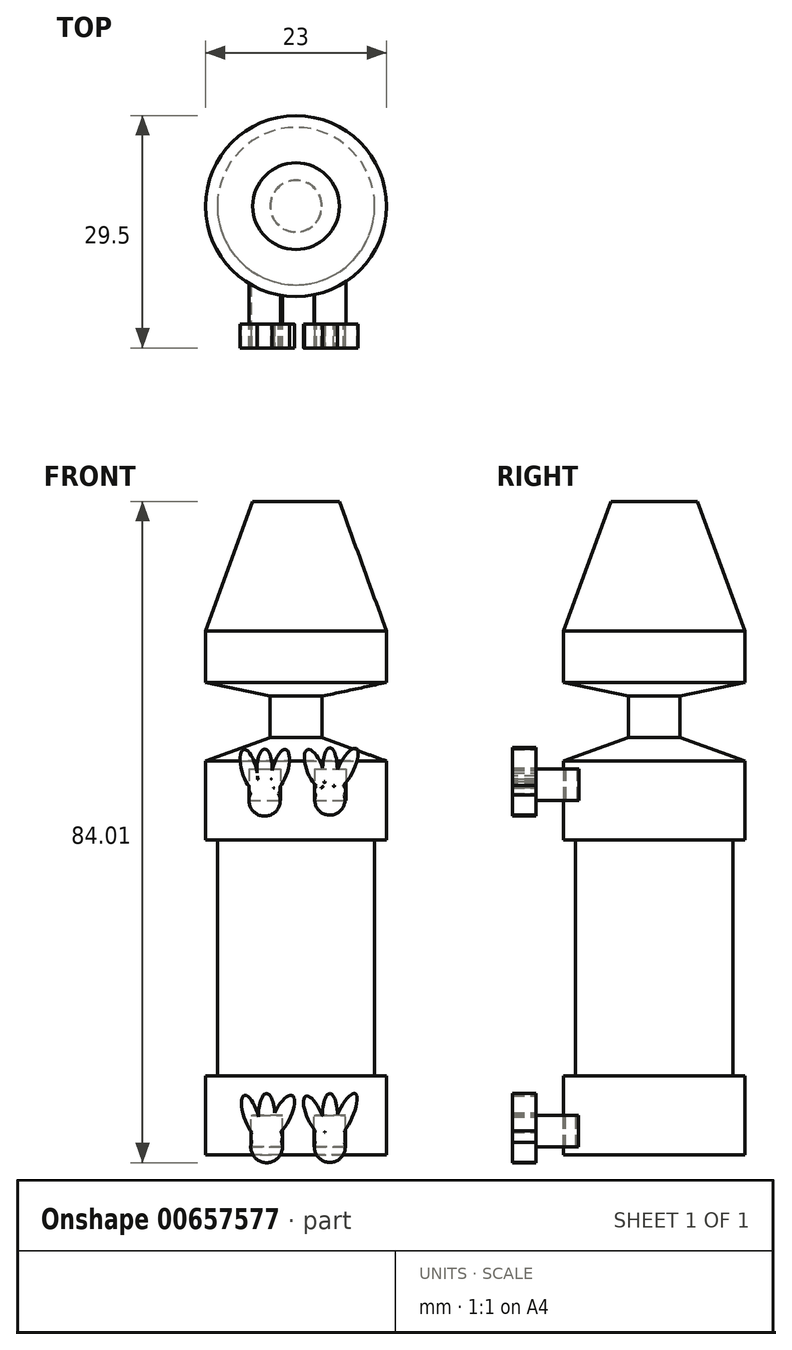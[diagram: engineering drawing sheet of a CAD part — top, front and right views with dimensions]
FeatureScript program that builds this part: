
annotation { "Feature Type Name" : "Feature", "Feature Type Description" : "" }
export const myFeature = defineFeature(function(context is Context, id is Id, definition is map)
    precondition{}
    {
        {
            var Q0;
            Q0=qCreatedBy(makeId("Top.planeOp"),FACE);
            var sketch = newSketch(context, id + "F0", { "sketchPlane" : qUnion([Q0])});
            skCircle(sketch, "E0", {"center": v(0, 0) * mm, "radius": 10 * mm});
            skSolve(sketch);
        }
        {
            var Q0;
            Q0 = qSketchRegion(id + "F0", true);
            extrude(context, id + "F1", {"entities" : qUnion([Q0]), "depth" : 40 * mm, "offsetDistance" : 25 * mm});
        }
        {
            var Q0;
            Q0=makeQuery(id+"F1.opExtrude","CAP_FACE",FACE,{"disambiguationData":[OSD([sQuery(id+"F0.wireOp",EDGE,"E0")])],"isStart":false});
            var sketch = newSketch(context, id + "F2", { "sketchPlane" : qUnion([Q0])});
            skCircle(sketch, "E1", {"center": v(0, 0) * mm, "radius": 11.5 * mm});
            skSolve(sketch);
        }
        {
            var Q0;
            Q0=makeQuery(id+"F2.imprint","IMPRINT",FACE,{"disambiguationData":[TD([[makeQuery(id+"F2.imprint","IMPRINT",EDGE,{"derivedFrom":sQuery(id+"F2.wireOp",EDGE,"E1")}),1.0]])]});
            var Q1;
            Q1=makeQuery(id+"F2.imprint","IMPRINT",FACE,{"disambiguationData":[TD([[makeQuery(id+"F2.imprint","IMPRINT",EDGE,{"derivedFrom":makeQuery(id+"F1.opExtrude","CAP_EDGE",EDGE,{"disambiguationData":[OSD([sQuery(id+"F0.wireOp",EDGE,"E0")])],"isStart":false})}),1.0]])]});
            extrude(context, id + "F3", {"entities" : qUnion([Q0, Q1]), "operationType" : NewBodyOperationType.ADD, "depth" : 5 * mm, "offsetDistance" : 25 * mm});
        }
        {
            var Q0;
            Q0=makeQuery(id+"F3.opExtrude","CAP_FACE",FACE,{"disambiguationData":[OSD([sQuery(id+"F2.wireOp",EDGE,"E1")])],"isStart":true});
            extrude(context, id + "F4", {"entities" : qUnion([Q0]), "operationType" : NewBodyOperationType.ADD, "depth" : 5 * mm, "offsetDistance" : 25 * mm});
        }
        {
            var Q0;
            Q0=makeQuery(id+"F1.opExtrude","CAP_FACE",FACE,{"disambiguationData":[OSD([sQuery(id+"F0.wireOp",EDGE,"E0")])],"isStart":true});
            var sketch = newSketch(context, id + "F5", { "sketchPlane" : qUnion([Q0])});
            skCircle(sketch, "E2", {"center": v(0, 0) * mm, "radius": 11.5 * mm});
            skSolve(sketch);
        }
        {
            var Q0;
            Q0 = qSketchRegion(id + "F5", true);
            extrude(context, id + "F6", {"entities" : qUnion([Q0]), "operationType" : NewBodyOperationType.ADD, "depth" : 5 * mm, "offsetDistance" : 25 * mm});
        }
        {
            var Q0;
            Q0=makeQuery(id+"F6.opExtrude","CAP_FACE",FACE,{"disambiguationData":[OSD([sQuery(id+"F5.wireOp",EDGE,"E2")])],"isStart":true});
            extrude(context, id + "F7", {"entities" : qUnion([Q0]), "operationType" : NewBodyOperationType.ADD, "depth" : 5 * mm, "offsetDistance" : 25 * mm});
        }
        {
            var Q0;
            Q0=makeQuery(id+"F2.imprint","IMPRINT",FACE,{"disambiguationData":[TD([[makeQuery(id+"F2.imprint","IMPRINT",EDGE,{"derivedFrom":makeQuery(id+"F1.opExtrude","CAP_EDGE",EDGE,{"disambiguationData":[OSD([sQuery(id+"F0.wireOp",EDGE,"E0")])],"isStart":false})}),1.0]])]});
            var sketch = newSketch(context, id + "F8", { "sketchPlane" : qUnion([Q0])});
            skLineSegment(sketch, "E3.bottom", {"start": v(-5.99, 0) * mm, "end": v(-1.99, 0) * mm});
            skLineSegment(sketch, "E3.top", {"start": v(-5.99, -15) * mm, "end": v(-1.99, -15) * mm});
            skLineSegment(sketch, "E3.left", {"start": v(-5.99, 0) * mm, "end": v(-5.99, -15) * mm});
            skLineSegment(sketch, "E3.right", {"start": v(-1.99, 0) * mm, "end": v(-1.99, -15) * mm});
            skLineSegment(sketch, "E4.bottom", {"start": v(2.36, 0) * mm, "end": v(6.36, 0) * mm});
            skLineSegment(sketch, "E4.top", {"start": v(2.36, -15) * mm, "end": v(6.36, -15) * mm});
            skLineSegment(sketch, "E4.left", {"start": v(2.36, 0) * mm, "end": v(2.36, -15) * mm});
            skLineSegment(sketch, "E4.right", {"start": v(6.36, 0) * mm, "end": v(6.36, -15) * mm});
            skSolve(sketch);
        }
        {
            var Q0;
            Q0 = qSketchRegion(id + "F8", true);
            extrude(context, id + "F9", {"entities" : qUnion([Q0]), "operationType" : NewBodyOperationType.ADD, "depth" : 4 * mm, "offsetDistance" : 25 * mm});
        }
        {
            var Q0;
            Q0=makeQuery(id+"F9.opExtrude","SWEPT_FACE",FACE,{"disambiguationData":[OSD([sQuery(id+"F8.wireOp",EDGE,"E3.top")])]});
            var sketch = newSketch(context, id + "F10", { "sketchPlane" : qUnion([Q0])});
            skCircle(sketch, "E5", {"center": v(-3.99, 40) * mm, "radius": 2 * mm});
            skEllipse(sketch, "E6", {"center": v(-5.99, 44) * mm, "majorRadius": 2.55 * mm, "minorRadius": 0.93 * mm, "majorAxis": v(-0.26, 0.97)});
            skEllipse(sketch, "E7", {"center": v(-3.99, 44) * mm, "majorRadius": 2.52 * mm, "minorRadius": 0.97 * mm, "majorAxis": v(0, 1)});
            skEllipse(sketch, "E8", {"center": v(-1.99, 44) * mm, "majorRadius": 2.56 * mm, "minorRadius": 0.96 * mm, "majorAxis": v(0.27, 0.96)});
            skEllipse(sketch, "E9", {"center": v(-3.99, 41.48) * mm, "majorRadius": 1.98 * mm, "minorRadius": 1.35 * mm, "majorAxis": v(-1, 0)});
            skCircle(sketch, "E10", {"center": v(4.3, 40.05) * mm, "radius": 1.92 * mm});
            skEllipse(sketch, "E11", {"center": v(2.36, 44.04) * mm, "majorRadius": 2.58 * mm, "minorRadius": 1 * mm, "majorAxis": v(-0.36, 0.93)});
            skEllipse(sketch, "E12", {"center": v(4.32, 43.98) * mm, "majorRadius": 2.73 * mm, "minorRadius": 0.93 * mm, "majorAxis": v(0, 1)});
            skEllipse(sketch, "E13", {"center": v(6.33, 44.02) * mm, "majorRadius": 2.89 * mm, "minorRadius": 0.95 * mm, "majorAxis": v(0.46, 0.9)});
            skEllipse(sketch, "E14", {"center": v(4.32, 41.25) * mm, "majorRadius": 1.97 * mm, "minorRadius": 1.26 * mm, "majorAxis": v(-1, 0)});
            skSolve(sketch);
        }
        {
            var Q0;
            {var subQ0=sQuery(id+"F10.wireOp",EDGE,"E9");var subQ1=sQuery(id+"F10.wireOp",EDGE,"E6");var subQ2=makeQuery(id+"F10.imprint","INTERSECT",VERTEX,{"disambiguationData":[OD(0.0)],"derivedFrom":[subQ1,subQ0]});Q0=makeQuery(id+"F10.imprint","IMPRINT",FACE,{"disambiguationData":[TD([[makeQuery(id+"F10.imprint","IMPRINT",EDGE,{"disambiguationData":[TD([[subQ2,-1.0]])],"derivedFrom":subQ1}),1.0]])]});}
            var Q1;
            {var subQ0=sQuery(id+"F10.wireOp",EDGE,"E7");var subQ1=sQuery(id+"F10.wireOp",EDGE,"E6");var subQ2=makeQuery(id+"F10.imprint","INTERSECT",VERTEX,{"disambiguationData":[OD(0.0)],"derivedFrom":[subQ1,subQ0]});Q1=makeQuery(id+"F10.imprint","IMPRINT",FACE,{"disambiguationData":[TD([[makeQuery(id+"F10.imprint","IMPRINT",EDGE,{"disambiguationData":[TD([[subQ2,-1.0]])],"derivedFrom":subQ1}),1.0]])]});}
            var Q2;
            {var subQ0=sQuery(id+"F10.wireOp",EDGE,"E8");var subQ1=sQuery(id+"F10.wireOp",EDGE,"E7");var subQ2=makeQuery(id+"F10.imprint","INTERSECT",VERTEX,{"disambiguationData":[OD(0.0)],"derivedFrom":[subQ1,subQ0]});Q2=makeQuery(id+"F10.imprint","IMPRINT",FACE,{"disambiguationData":[TD([[makeQuery(id+"F10.imprint","IMPRINT",EDGE,{"disambiguationData":[TD([[subQ2,-1.0]])],"derivedFrom":subQ1}),1.0]])]});}
            var Q3;
            {var subQ0=sQuery(id+"F10.wireOp",EDGE,"E9");var subQ1=sQuery(id+"F10.wireOp",EDGE,"E5");var subQ2=makeQuery(id+"F10.imprint","INTERSECT",VERTEX,{"disambiguationData":[OD(0.0)],"derivedFrom":[subQ1,subQ0]});Q3=makeQuery(id+"F10.imprint","IMPRINT",FACE,{"disambiguationData":[TD([[makeQuery(id+"F10.imprint","IMPRINT",EDGE,{"disambiguationData":[TD([[subQ2,-1.0]])],"derivedFrom":subQ1}),-1.0]])]});}
            var Q4;
            {var subQ0=sQuery(id+"F10.wireOp",EDGE,"E8");var subQ1=sQuery(id+"F10.wireOp",EDGE,"E5");var subQ2=makeQuery(id+"F10.imprint","INTERSECT",VERTEX,{"disambiguationData":[OD(0.0)],"derivedFrom":[subQ1,subQ0]});Q4=makeQuery(id+"F10.imprint","IMPRINT",FACE,{"disambiguationData":[TD([[makeQuery(id+"F10.imprint","IMPRINT",EDGE,{"disambiguationData":[TD([[subQ2,-1.0]])],"derivedFrom":subQ1}),-1.0]])]});}
            var Q5;
            {var subQ3=sQuery(id+"F10.wireOp",EDGE,"E7");var subQ5=sQuery(id+"F10.wireOp",EDGE,"E5");var subQ6=makeQuery(id+"F10.imprint","INTERSECT",VERTEX,{"disambiguationData":[OD(1.0)],"derivedFrom":[subQ5,subQ3]});Q5=makeQuery(id+"F10.imprint","IMPRINT",FACE,{"disambiguationData":[TD([[makeQuery(id+"F10.imprint","IMPRINT",EDGE,{"disambiguationData":[TD([[subQ6,-1.0]])],"derivedFrom":subQ5}),-1.0]])]});}
            var Q6;
            {var subQ1=sQuery(id+"F10.wireOp",EDGE,"E5");var subQ3=sQuery(id+"F10.wireOp",EDGE,"E9");var subQ8=makeQuery(id+"F10.imprint","INTERSECT",VERTEX,{"disambiguationData":[OD(0.0)],"derivedFrom":[subQ1,subQ3]});Q6=makeQuery(id+"F10.imprint","IMPRINT",FACE,{"disambiguationData":[TD([[makeQuery(id+"F10.imprint","IMPRINT",EDGE,{"disambiguationData":[TD([[subQ8,-1.0]])],"derivedFrom":subQ1}),1.0]])]});}
            var Q7;
            {var subQ0=sQuery(id+"F10.wireOp",EDGE,"E5");var subQ1=makeQuery(id+"F9.opExtrude","CAP_EDGE",EDGE,{"disambiguationData":[OSD([sQuery(id+"F8.wireOp",EDGE,"E3.top")])],"isStart":true});var subQ2=makeQuery(id+"F10.imprint","INTERSECT",VERTEX,{"disambiguationData":[OD(0.0)],"derivedFrom":[subQ1,subQ0]});Q7=makeQuery(id+"F10.imprint","IMPRINT",FACE,{"disambiguationData":[TD([[makeQuery(id+"F10.imprint","IMPRINT",EDGE,{"disambiguationData":[TD([[subQ2,1.0]])],"derivedFrom":subQ0}),1.0]])]});}
            var Q8;
            {var subQ0=sQuery(id+"F10.wireOp",EDGE,"E7");var subQ1=makeQuery(id+"F9.opExtrude","CAP_EDGE",EDGE,{"disambiguationData":[OSD([sQuery(id+"F8.wireOp",EDGE,"E3.top")])],"isStart":false});var subQ2=makeQuery(id+"F10.imprint","INTERSECT",VERTEX,{"disambiguationData":[OD(0.0)],"derivedFrom":[subQ1,subQ0]});Q8=makeQuery(id+"F10.imprint","IMPRINT",FACE,{"disambiguationData":[TD([[makeQuery(id+"F10.imprint","IMPRINT",EDGE,{"disambiguationData":[TD([[subQ2,1.0]])],"derivedFrom":subQ0}),1.0]])]});}
            var Q9;
            {var subQ0=sQuery(id+"F10.wireOp",EDGE,"E9");var subQ1=sQuery(id+"F10.wireOp",EDGE,"E5");var subQ2=makeQuery(id+"F10.imprint","INTERSECT",VERTEX,{"disambiguationData":[OD(0.0)],"derivedFrom":[subQ1,subQ0]});Q9=makeQuery(id+"F10.imprint","IMPRINT",FACE,{"disambiguationData":[TD([[makeQuery(id+"F10.imprint","IMPRINT",EDGE,{"disambiguationData":[TD([[subQ2,1.0]])],"derivedFrom":subQ1}),1.0]])]});}
            var Q10;
            {var subQ0=sQuery(id+"F10.wireOp",EDGE,"E6");var subQ1=sQuery(id+"F8.wireOp",EDGE,"E3.top");var subQ4=makeQuery(id+"F9.opExtrude","CAP_EDGE",EDGE,{"disambiguationData":[OSD([subQ1])],"isStart":false});var subQ5=makeQuery(id+"F10.imprint","INTERSECT",VERTEX,{"derivedFrom":[subQ4,subQ0]});Q10=makeQuery(id+"F10.imprint","IMPRINT",FACE,{"disambiguationData":[TD([[makeQuery(id+"F10.imprint","IMPRINT",EDGE,{"disambiguationData":[TD([[subQ5,-1.0]])],"derivedFrom":subQ0}),1.0]])]});}
            var Q11;
            {var subQ1=sQuery(id+"F10.wireOp",EDGE,"E6");var subQ7=sQuery(id+"F10.wireOp",EDGE,"E9");var subQ8=makeQuery(id+"F10.imprint","INTERSECT",VERTEX,{"disambiguationData":[OD(1.0)],"derivedFrom":[subQ1,subQ7]});Q11=makeQuery(id+"F10.imprint","IMPRINT",FACE,{"disambiguationData":[TD([[makeQuery(id+"F10.imprint","IMPRINT",EDGE,{"disambiguationData":[TD([[subQ8,-1.0]])],"derivedFrom":subQ1}),1.0]])]});}
            var Q12;
            {var subQ1=sQuery(id+"F10.wireOp",EDGE,"E8");var subQ6=sQuery(id+"F10.wireOp",EDGE,"E7");var subQ10=makeQuery(id+"F10.imprint","INTERSECT",VERTEX,{"disambiguationData":[OD(0.0)],"derivedFrom":[subQ6,subQ1]});Q12=makeQuery(id+"F10.imprint","IMPRINT",FACE,{"disambiguationData":[TD([[makeQuery(id+"F10.imprint","IMPRINT",EDGE,{"disambiguationData":[TD([[subQ10,-1.0]])],"derivedFrom":subQ6}),-1.0]])]});}
            var Q13;
            {var subQ0=sQuery(id+"F10.wireOp",EDGE,"E8");var subQ1=sQuery(id+"F8.wireOp",EDGE,"E3.top");var subQ2=makeQuery(id+"F9.opExtrude","CAP_EDGE",EDGE,{"disambiguationData":[OSD([subQ1])],"isStart":false});var subQ3=makeQuery(id+"F10.imprint","INTERSECT",VERTEX,{"derivedFrom":[subQ2,subQ0]});Q13=makeQuery(id+"F10.imprint","IMPRINT",FACE,{"disambiguationData":[TD([[makeQuery(id+"F10.imprint","IMPRINT",EDGE,{"disambiguationData":[TD([[subQ3,1.0]])],"derivedFrom":subQ0}),1.0]])]});}
            var Q14;
            {var subQ1=sQuery(id+"F10.wireOp",EDGE,"E7");var subQ5=sQuery(id+"F10.wireOp",EDGE,"E6");var subQ11=makeQuery(id+"F10.imprint","INTERSECT",VERTEX,{"disambiguationData":[OD(0.0)],"derivedFrom":[subQ5,subQ1]});Q14=makeQuery(id+"F10.imprint","IMPRINT",FACE,{"disambiguationData":[TD([[makeQuery(id+"F10.imprint","IMPRINT",EDGE,{"disambiguationData":[TD([[subQ11,-1.0]])],"derivedFrom":subQ5}),-1.0]])]});}
            var Q15;
            {var subQ0=sQuery(id+"F10.wireOp",EDGE,"E7");var subQ1=sQuery(id+"F10.wireOp",EDGE,"E5");var subQ2=makeQuery(id+"F10.imprint","INTERSECT",VERTEX,{"disambiguationData":[OD(0.0)],"derivedFrom":[subQ1,subQ0]});Q15=makeQuery(id+"F10.imprint","IMPRINT",FACE,{"disambiguationData":[TD([[makeQuery(id+"F10.imprint","IMPRINT",EDGE,{"disambiguationData":[TD([[subQ2,-1.0]])],"derivedFrom":subQ1}),-1.0]])]});}
            var Q16;
            {var subQ0=sQuery(id+"F10.wireOp",EDGE,"E8");var subQ1=sQuery(id+"F10.wireOp",EDGE,"E5");var subQ2=makeQuery(id+"F10.imprint","INTERSECT",VERTEX,{"disambiguationData":[OD(1.0)],"derivedFrom":[subQ1,subQ0]});Q16=makeQuery(id+"F10.imprint","IMPRINT",FACE,{"disambiguationData":[TD([[makeQuery(id+"F10.imprint","IMPRINT",EDGE,{"disambiguationData":[TD([[subQ2,-1.0]])],"derivedFrom":subQ1}),-1.0]])]});}
            var Q17;
            {var subQ0=sQuery(id+"F10.wireOp",EDGE,"E7");var subQ1=sQuery(id+"F10.wireOp",EDGE,"E5");var subQ2=makeQuery(id+"F10.imprint","INTERSECT",VERTEX,{"disambiguationData":[OD(0.0)],"derivedFrom":[subQ1,subQ0]});Q17=makeQuery(id+"F10.imprint","IMPRINT",FACE,{"disambiguationData":[TD([[makeQuery(id+"F10.imprint","IMPRINT",EDGE,{"disambiguationData":[TD([[subQ2,-1.0]])],"derivedFrom":subQ1}),1.0]])]});}
            var Q18;
            {var subQ0=sQuery(id+"F10.wireOp",EDGE,"E13");var subQ1=sQuery(id+"F10.wireOp",EDGE,"E12");var subQ2=makeQuery(id+"F10.imprint","INTERSECT",VERTEX,{"disambiguationData":[OD(0.0)],"derivedFrom":[subQ1,subQ0]});Q18=makeQuery(id+"F10.imprint","IMPRINT",FACE,{"disambiguationData":[TD([[makeQuery(id+"F10.imprint","IMPRINT",EDGE,{"disambiguationData":[TD([[subQ2,1.0]])],"derivedFrom":subQ1}),-1.0]])]});}
            var Q19;
            {var subQ0=sQuery(id+"F10.wireOp",EDGE,"E13");var subQ1=sQuery(id+"F10.wireOp",EDGE,"E12");var subQ2=makeQuery(id+"F10.imprint","INTERSECT",VERTEX,{"disambiguationData":[OD(0.0)],"derivedFrom":[subQ1,subQ0]});Q19=makeQuery(id+"F10.imprint","IMPRINT",FACE,{"disambiguationData":[TD([[makeQuery(id+"F10.imprint","IMPRINT",EDGE,{"disambiguationData":[TD([[subQ2,1.0]])],"derivedFrom":subQ1}),1.0]])]});}
            var Q20;
            {var subQ0=sQuery(id+"F10.wireOp",EDGE,"E13");var subQ1=sQuery(id+"F10.wireOp",EDGE,"E10");var subQ2=makeQuery(id+"F10.imprint","INTERSECT",VERTEX,{"disambiguationData":[OD(0.0)],"derivedFrom":[subQ1,subQ0]});Q20=makeQuery(id+"F10.imprint","IMPRINT",FACE,{"disambiguationData":[TD([[makeQuery(id+"F10.imprint","IMPRINT",EDGE,{"disambiguationData":[TD([[subQ2,-1.0]])],"derivedFrom":subQ1}),-1.0]])]});}
            var Q21;
            {var subQ0=sQuery(id+"F10.wireOp",EDGE,"E12");var subQ1=sQuery(id+"F10.wireOp",EDGE,"E10");var subQ2=makeQuery(id+"F10.imprint","INTERSECT",VERTEX,{"disambiguationData":[OD(0.0)],"derivedFrom":[subQ1,subQ0]});Q21=makeQuery(id+"F10.imprint","IMPRINT",FACE,{"disambiguationData":[TD([[makeQuery(id+"F10.imprint","IMPRINT",EDGE,{"disambiguationData":[TD([[subQ2,-1.0]])],"derivedFrom":subQ1}),-1.0]])]});}
            var Q22;
            {var subQ0=sQuery(id+"F10.wireOp",EDGE,"E13");var subQ1=sQuery(id+"F10.wireOp",EDGE,"E10");var subQ2=makeQuery(id+"F10.imprint","INTERSECT",VERTEX,{"disambiguationData":[OD(0.0)],"derivedFrom":[subQ1,subQ0]});Q22=makeQuery(id+"F10.imprint","IMPRINT",FACE,{"disambiguationData":[TD([[makeQuery(id+"F10.imprint","IMPRINT",EDGE,{"disambiguationData":[TD([[subQ2,-1.0]])],"derivedFrom":subQ1}),1.0]])]});}
            var Q23;
            {var subQ0=sQuery(id+"F10.wireOp",EDGE,"E13");var subQ1=sQuery(id+"F10.wireOp",EDGE,"E10");var subQ2=makeQuery(id+"F10.imprint","INTERSECT",VERTEX,{"disambiguationData":[OD(1.0)],"derivedFrom":[subQ1,subQ0]});Q23=makeQuery(id+"F10.imprint","IMPRINT",FACE,{"disambiguationData":[TD([[makeQuery(id+"F10.imprint","IMPRINT",EDGE,{"disambiguationData":[TD([[subQ2,-1.0]])],"derivedFrom":subQ1}),1.0]])]});}
            var Q24;
            {var subQ1=sQuery(id+"F10.wireOp",EDGE,"E10");var subQ7=sQuery(id+"F10.wireOp",EDGE,"E13");var subQ8=makeQuery(id+"F10.imprint","INTERSECT",VERTEX,{"disambiguationData":[OD(1.0)],"derivedFrom":[subQ1,subQ7]});Q24=makeQuery(id+"F10.imprint","IMPRINT",FACE,{"disambiguationData":[TD([[makeQuery(id+"F10.imprint","IMPRINT",EDGE,{"disambiguationData":[TD([[subQ8,-1.0]])],"derivedFrom":subQ1}),-1.0]])]});}
            var Q25;
            {var subQ0=sQuery(id+"F10.wireOp",EDGE,"E12");var subQ1=sQuery(id+"F10.wireOp",EDGE,"E11");var subQ2=makeQuery(id+"F10.imprint","INTERSECT",VERTEX,{"disambiguationData":[OD(0.0)],"derivedFrom":[subQ1,subQ0]});Q25=makeQuery(id+"F10.imprint","IMPRINT",FACE,{"disambiguationData":[TD([[makeQuery(id+"F10.imprint","IMPRINT",EDGE,{"disambiguationData":[TD([[subQ2,1.0]])],"derivedFrom":subQ1}),-1.0]])]});}
            var Q26;
            {var subQ1=sQuery(id+"F10.wireOp",EDGE,"E11");var subQ3=sQuery(id+"F10.wireOp",EDGE,"E10");var subQ8=makeQuery(id+"F10.imprint","INTERSECT",VERTEX,{"disambiguationData":[OD(0.0)],"derivedFrom":[subQ3,subQ1]});Q26=makeQuery(id+"F10.imprint","IMPRINT",FACE,{"disambiguationData":[TD([[makeQuery(id+"F10.imprint","IMPRINT",EDGE,{"disambiguationData":[TD([[subQ8,-1.0]])],"derivedFrom":subQ3}),-1.0]])]});}
            var Q27;
            {var subQ0=sQuery(id+"F10.wireOp",EDGE,"E14");var subQ1=sQuery(id+"F10.wireOp",EDGE,"E11");var subQ2=makeQuery(id+"F10.imprint","INTERSECT",VERTEX,{"disambiguationData":[OD(0.0)],"derivedFrom":[subQ1,subQ0]});Q27=makeQuery(id+"F10.imprint","IMPRINT",FACE,{"disambiguationData":[TD([[makeQuery(id+"F10.imprint","IMPRINT",EDGE,{"disambiguationData":[TD([[subQ2,1.0]])],"derivedFrom":subQ1}),1.0]])]});}
            var Q28;
            {var subQ0=sQuery(id+"F10.wireOp",EDGE,"E14");var subQ1=sQuery(id+"F10.wireOp",EDGE,"E10");var subQ2=makeQuery(id+"F10.imprint","INTERSECT",VERTEX,{"disambiguationData":[OD(1.0)],"derivedFrom":[subQ1,subQ0]});Q28=makeQuery(id+"F10.imprint","IMPRINT",FACE,{"disambiguationData":[TD([[makeQuery(id+"F10.imprint","IMPRINT",EDGE,{"disambiguationData":[TD([[subQ2,1.0]])],"derivedFrom":subQ1}),-1.0]])]});}
            var Q29;
            {var subQ0=sQuery(id+"F10.wireOp",EDGE,"E14");var subQ1=sQuery(id+"F10.wireOp",EDGE,"E10");var subQ9=makeQuery(id+"F10.imprint","INTERSECT",VERTEX,{"disambiguationData":[OD(0.0)],"derivedFrom":[subQ1,subQ0]});Q29=makeQuery(id+"F10.imprint","IMPRINT",FACE,{"disambiguationData":[TD([[makeQuery(id+"F10.imprint","IMPRINT",EDGE,{"disambiguationData":[TD([[subQ9,-1.0]])],"derivedFrom":subQ1}),1.0]])]});}
            var Q30;
            {var subQ0=sQuery(id+"F10.wireOp",EDGE,"E14");var subQ1=sQuery(id+"F10.wireOp",EDGE,"E10");var subQ2=makeQuery(id+"F10.imprint","INTERSECT",VERTEX,{"disambiguationData":[OD(0.0)],"derivedFrom":[subQ1,subQ0]});Q30=makeQuery(id+"F10.imprint","IMPRINT",FACE,{"disambiguationData":[TD([[makeQuery(id+"F10.imprint","IMPRINT",EDGE,{"disambiguationData":[TD([[subQ2,-1.0]])],"derivedFrom":subQ1}),-1.0]])]});}
            var Q31;
            {var subQ0=sQuery(id+"F10.wireOp",EDGE,"E14");var subQ1=sQuery(id+"F10.wireOp",EDGE,"E10");var subQ2=makeQuery(id+"F10.imprint","INTERSECT",VERTEX,{"disambiguationData":[OD(0.0)],"derivedFrom":[subQ1,subQ0]});Q31=makeQuery(id+"F10.imprint","IMPRINT",FACE,{"disambiguationData":[TD([[makeQuery(id+"F10.imprint","IMPRINT",EDGE,{"disambiguationData":[TD([[subQ2,1.0]])],"derivedFrom":subQ1}),1.0]])]});}
            var Q32;
            {var subQ0=sQuery(id+"F10.wireOp",EDGE,"E12");var subQ1=sQuery(id+"F10.wireOp",EDGE,"E11");var subQ2=makeQuery(id+"F10.imprint","INTERSECT",VERTEX,{"disambiguationData":[OD(0.0)],"derivedFrom":[subQ1,subQ0]});Q32=makeQuery(id+"F10.imprint","IMPRINT",FACE,{"disambiguationData":[TD([[makeQuery(id+"F10.imprint","IMPRINT",EDGE,{"disambiguationData":[TD([[subQ2,1.0]])],"derivedFrom":subQ1}),1.0]])]});}
            var Q33;
            {var subQ0=sQuery(id+"F10.wireOp",EDGE,"E12");var subQ1=sQuery(id+"F10.wireOp",EDGE,"E10");var subQ2=makeQuery(id+"F10.imprint","INTERSECT",VERTEX,{"disambiguationData":[OD(1.0)],"derivedFrom":[subQ1,subQ0]});Q33=makeQuery(id+"F10.imprint","IMPRINT",FACE,{"disambiguationData":[TD([[makeQuery(id+"F10.imprint","IMPRINT",EDGE,{"disambiguationData":[TD([[subQ2,-1.0]])],"derivedFrom":subQ1}),-1.0]])]});}
            extrude(context, id + "F11", {"entities" : qUnion([Q0, Q1, Q2, Q3, Q4, Q5, Q6, Q7, Q8, Q9, Q10, Q11, Q12, Q13, Q14, Q15, Q16, Q17, Q18, Q19, Q20, Q21, Q22, Q23, Q24, Q25, Q26, Q27, Q28, Q29, Q30, Q31, Q32, Q33]), "operationType" : NewBodyOperationType.ADD, "depth" : 3 * mm, "offsetDistance" : 25 * mm});
        }
        {
            var Q0;
            Q0=makeQuery(id+"F3.opExtrude","CAP_FACE",FACE,{"disambiguationData":[OSD([sQuery(id+"F2.wireOp",EDGE,"E1")])],"isStart":false});
            var sketch = newSketch(context, id + "F12", { "sketchPlane" : qUnion([Q0])});
            skCircle(sketch, "E15", {"center": v(0, 0) * mm, "radius": 11.5 * mm});
            skSolve(sketch);
        }
        {
            var Q0;
            Q0 = qSketchRegion(id + "F12", true);
            extrude(context, id + "F13", {"entities" : qUnion([Q0]), "operationType" : NewBodyOperationType.ADD, "depth" : 3 * mm, "offsetDistance" : 25 * mm, "hasDraft" : true, "draftAngle" : 70 * degree, "draftPullDirection" : true});
        }
        {
            var Q0;
            Q0=makeQuery(id+"F13.opExtrude","CAP_FACE",FACE,{"disambiguationData":[OSD([sQuery(id+"F12.wireOp",EDGE,"E15")])],"isStart":false});
            var sketch = newSketch(context, id + "F14", { "sketchPlane" : qUnion([Q0])});
            skCircle(sketch, "E16", {"center": v(0, 0) * mm, "radius": 3.3 * mm});
            skSolve(sketch);
        }
        {
            var Q0;
            Q0 = qSketchRegion(id + "F14", true);
            extrude(context, id + "F15", {"entities" : qUnion([Q0]), "operationType" : NewBodyOperationType.ADD, "depth" : 5 * mm, "offsetDistance" : 25 * mm});
        }
        {
            var Q0;
            Q0=makeQuery(id+"F15.opExtrude","CAP_FACE",FACE,{"disambiguationData":[OSD([sQuery(id+"F14.wireOp",EDGE,"E16")])],"isStart":false});
            var sketch = newSketch(context, id + "F16", { "sketchPlane" : qUnion([Q0])});
            skCircle(sketch, "E17", {"center": v(0, 0) * mm, "radius": 11.5 * mm});
            skSolve(sketch);
        }
        {
            var Q0;
            Q0 = qSketchRegion(id + "F16", true);
            extrude(context, id + "F17", {"entities" : qUnion([Q0]), "operationType" : NewBodyOperationType.ADD, "depth" : 25 * mm, "offsetDistance" : 25 * mm});
        }
        {
            var Q0;
            Q0=makeQuery(id+"F17.opExtrude","CAP_EDGE",EDGE,{"disambiguationData":[OSD([sQuery(id+"F16.wireOp",EDGE,"E17")])],"isStart":true});
            chamfer(context, id + "F18", {"entities" : qUnion([Q0]), "chamferType" : ChamferType.OFFSET_ANGLE, "width" : 2 * mm, "oppositeDirection" : false, "angle" : 78 * degree, "tangentPropagation" : true});
        }
        {
            var Q0;
            Q0=makeQuery(id+"F17.opExtrude","CAP_EDGE",EDGE,{"disambiguationData":[OSD([sQuery(id+"F16.wireOp",EDGE,"E17")])],"isStart":false});
            chamfer(context, id + "F19", {"entities" : qUnion([Q0]), "chamferType" : ChamferType.OFFSET_ANGLE, "width" : 6 * mm, "oppositeDirection" : false, "angle" : 70 * degree, "tangentPropagation" : true});
        }
        {
            var Q0;
            Q0=makeQuery(id+"F5.imprint","IMPRINT",FACE,{"disambiguationData":[TD([[makeQuery(id+"F5.imprint","IMPRINT",EDGE,{"derivedFrom":makeQuery(id+"F1.opExtrude","CAP_EDGE",EDGE,{"disambiguationData":[OSD([sQuery(id+"F0.wireOp",EDGE,"E0")])],"isStart":true})}),-1.0]])]});
            var sketch = newSketch(context, id + "F20", { "sketchPlane" : qUnion([Q0])});
            skLineSegment(sketch, "E18.bottom", {"start": v(-5.74, 0) * mm, "end": v(-1.74, 0) * mm});
            skLineSegment(sketch, "E18.top", {"start": v(-5.74, 15) * mm, "end": v(-1.74, 15) * mm});
            skLineSegment(sketch, "E18.left", {"start": v(-5.74, 0) * mm, "end": v(-5.74, 15) * mm});
            skLineSegment(sketch, "E18.right", {"start": v(-1.74, 0) * mm, "end": v(-1.74, 15) * mm});
            skLineSegment(sketch, "E19.bottom", {"start": v(2.26, 0) * mm, "end": v(6.26, 0) * mm});
            skLineSegment(sketch, "E19.top", {"start": v(2.26, 15) * mm, "end": v(6.26, 15) * mm});
            skLineSegment(sketch, "E19.left", {"start": v(2.26, 0) * mm, "end": v(2.26, 15) * mm});
            skLineSegment(sketch, "E19.right", {"start": v(6.26, 0) * mm, "end": v(6.26, 15) * mm});
            skSolve(sketch);
        }
        {
            var Q0;
            Q0 = qSketchRegion(id + "F20", true);
            extrude(context, id + "F21", {"entities" : qUnion([Q0]), "operationType" : NewBodyOperationType.ADD, "depth" : 4 * mm, "offsetDistance" : 25 * mm});
        }
        {
            var Q0;
            Q0=makeQuery(id+"F21.opExtrude","SWEPT_FACE",FACE,{"disambiguationData":[OSD([sQuery(id+"F20.wireOp",EDGE,"E18.top")])]});
            var sketch = newSketch(context, id + "F22", { "sketchPlane" : qUnion([Q0])});
            skCircle(sketch, "E20", {"center": v(-3.74, -4) * mm, "radius": 2.01 * mm});
            skCircle(sketch, "E21", {"center": v(4.3, -4) * mm, "radius": 1.97 * mm});
            skEllipse(sketch, "E22", {"center": v(-5.74, 0) * mm, "majorRadius": 2.68 * mm, "minorRadius": 0.9 * mm, "majorAxis": v(-0.3, 0.95)});
            skEllipse(sketch, "E23", {"center": v(-3.74, 0) * mm, "majorRadius": 2.77 * mm, "minorRadius": 1.02 * mm, "majorAxis": v(0, 1)});
            skEllipse(sketch, "E24", {"center": v(-1.74, 0) * mm, "majorRadius": 2.8 * mm, "minorRadius": 1.03 * mm, "majorAxis": v(0.45, 0.9)});
            skEllipse(sketch, "E25", {"center": v(-3.74, -2.77) * mm, "majorRadius": 2 * mm, "minorRadius": 1.67 * mm, "majorAxis": v(-1, 0)});
            skPoint(sketch, "E25.majorAxisSnap0", {"position": v(-3.74, -2.77) * mm});
            skPoint(sketch, "E25.majorAxisSnap1", {"position": v(-5.74, -2) * mm});
            skEllipse(sketch, "E26", {"center": v(2.32, 0) * mm, "majorRadius": 2.66 * mm, "minorRadius": 0.93 * mm, "majorAxis": v(-0.4, 0.91)});
            skEllipse(sketch, "E27", {"center": v(4.3, 0) * mm, "majorRadius": 2.77 * mm, "minorRadius": 0.96 * mm, "majorAxis": v(0, 1)});
            skEllipse(sketch, "E28", {"center": v(6.23, 0) * mm, "majorRadius": 3.05 * mm, "minorRadius": 0.93 * mm, "majorAxis": v(0.42, 0.9)});
            skEllipse(sketch, "E29", {"center": v(4.3, -2.77) * mm, "majorRadius": 1.96 * mm, "minorRadius": 2.63 * mm, "majorAxis": v(-1, 0)});
            skSolve(sketch);
        }
        {
            var Q0;
            Q0 = qSketchRegion(id + "F22", true);
            var Q1;
            {var subQ0=sQuery(id+"F22.wireOp",EDGE,"E24");var subQ1=sQuery(id+"F22.wireOp",EDGE,"E20");var subQ2=makeQuery(id+"F22.imprint","INTERSECT",VERTEX,{"disambiguationData":[OD(1.0)],"derivedFrom":[subQ1,subQ0]});Q1=makeQuery(id+"F22.imprint","IMPRINT",FACE,{"disambiguationData":[TD([[makeQuery(id+"F22.imprint","IMPRINT",EDGE,{"disambiguationData":[TD([[subQ2,-1.0]])],"derivedFrom":subQ1}),-1.0]])]});}
            var Q2;
            {var subQ0=sQuery(id+"F22.wireOp",EDGE,"E23");var subQ1=sQuery(id+"F22.wireOp",EDGE,"E20");var subQ2=makeQuery(id+"F22.imprint","INTERSECT",VERTEX,{"disambiguationData":[OD(0.0)],"derivedFrom":[subQ1,subQ0]});Q2=makeQuery(id+"F22.imprint","IMPRINT",FACE,{"disambiguationData":[TD([[makeQuery(id+"F22.imprint","IMPRINT",EDGE,{"disambiguationData":[TD([[subQ2,-1.0]])],"derivedFrom":subQ1}),-1.0]])]});}
            var Q3;
            {var subQ0=sQuery(id+"F22.wireOp",EDGE,"E24");var subQ1=sQuery(id+"F22.wireOp",EDGE,"E20");var subQ2=makeQuery(id+"F22.imprint","INTERSECT",VERTEX,{"disambiguationData":[OD(0.0)],"derivedFrom":[subQ1,subQ0]});Q3=makeQuery(id+"F22.imprint","IMPRINT",FACE,{"disambiguationData":[TD([[makeQuery(id+"F22.imprint","IMPRINT",EDGE,{"disambiguationData":[TD([[subQ2,-1.0]])],"derivedFrom":subQ1}),1.0]])]});}
            var Q4;
            {var subQ0=sQuery(id+"F22.wireOp",EDGE,"E23");var subQ1=sQuery(id+"F22.wireOp",EDGE,"E20");var subQ2=makeQuery(id+"F22.imprint","INTERSECT",VERTEX,{"disambiguationData":[OD(0.0)],"derivedFrom":[subQ1,subQ0]});Q4=makeQuery(id+"F22.imprint","IMPRINT",FACE,{"disambiguationData":[TD([[makeQuery(id+"F22.imprint","IMPRINT",EDGE,{"disambiguationData":[TD([[subQ2,-1.0]])],"derivedFrom":subQ1}),1.0]])]});}
            var Q5;
            {var subQ0=sQuery(id+"F22.wireOp",EDGE,"E24");var subQ1=sQuery(id+"F22.wireOp",EDGE,"E20");var subQ2=makeQuery(id+"F22.imprint","INTERSECT",VERTEX,{"disambiguationData":[OD(1.0)],"derivedFrom":[subQ1,subQ0]});Q5=makeQuery(id+"F22.imprint","IMPRINT",FACE,{"disambiguationData":[TD([[makeQuery(id+"F22.imprint","IMPRINT",EDGE,{"disambiguationData":[TD([[subQ2,-1.0]])],"derivedFrom":subQ1}),1.0]])]});}
            var Q6;
            {var subQ0=sQuery(id+"F22.wireOp",EDGE,"E23");var subQ1=sQuery(id+"F22.wireOp",EDGE,"E20");var subQ2=makeQuery(id+"F22.imprint","INTERSECT",VERTEX,{"disambiguationData":[OD(1.0)],"derivedFrom":[subQ1,subQ0]});Q6=makeQuery(id+"F22.imprint","IMPRINT",FACE,{"disambiguationData":[TD([[makeQuery(id+"F22.imprint","IMPRINT",EDGE,{"disambiguationData":[TD([[subQ2,-1.0]])],"derivedFrom":subQ1}),-1.0]])]});}
            var Q7;
            {var subQ0=sQuery(id+"F22.wireOp",EDGE,"E22");var subQ1=sQuery(id+"F22.wireOp",EDGE,"E20");var subQ2=makeQuery(id+"F22.imprint","INTERSECT",VERTEX,{"disambiguationData":[OD(0.0)],"derivedFrom":[subQ1,subQ0]});Q7=makeQuery(id+"F22.imprint","IMPRINT",FACE,{"disambiguationData":[TD([[makeQuery(id+"F22.imprint","IMPRINT",EDGE,{"disambiguationData":[TD([[subQ2,-1.0]])],"derivedFrom":subQ1}),1.0]])]});}
            var Q8;
            {var subQ0=sQuery(id+"F22.wireOp",EDGE,"E23");var subQ1=sQuery(id+"F22.wireOp",EDGE,"E22");var subQ2=makeQuery(id+"F22.imprint","INTERSECT",VERTEX,{"disambiguationData":[OD(0.0)],"derivedFrom":[subQ1,subQ0]});Q8=makeQuery(id+"F22.imprint","IMPRINT",FACE,{"disambiguationData":[TD([[makeQuery(id+"F22.imprint","IMPRINT",EDGE,{"disambiguationData":[TD([[subQ2,-1.0]])],"derivedFrom":subQ1}),1.0]])]});}
            var Q9;
            {var subQ0=sQuery(id+"F22.wireOp",EDGE,"E28");var subQ1=sQuery(id+"F22.wireOp",EDGE,"E21");var subQ2=makeQuery(id+"F22.imprint","INTERSECT",VERTEX,{"disambiguationData":[OD(1.0)],"derivedFrom":[subQ1,subQ0]});Q9=makeQuery(id+"F22.imprint","IMPRINT",FACE,{"disambiguationData":[TD([[makeQuery(id+"F22.imprint","IMPRINT",EDGE,{"disambiguationData":[TD([[subQ2,-1.0]])],"derivedFrom":subQ1}),-1.0]])]});}
            var Q10;
            {var subQ0=sQuery(id+"F22.wireOp",EDGE,"E27");var subQ1=sQuery(id+"F22.wireOp",EDGE,"E21");var subQ2=makeQuery(id+"F22.imprint","INTERSECT",VERTEX,{"disambiguationData":[OD(0.0)],"derivedFrom":[subQ1,subQ0]});Q10=makeQuery(id+"F22.imprint","IMPRINT",FACE,{"disambiguationData":[TD([[makeQuery(id+"F22.imprint","IMPRINT",EDGE,{"disambiguationData":[TD([[subQ2,-1.0]])],"derivedFrom":subQ1}),-1.0]])]});}
            var Q11;
            {var subQ0=sQuery(id+"F22.wireOp",EDGE,"E28");var subQ1=sQuery(id+"F22.wireOp",EDGE,"E21");var subQ2=makeQuery(id+"F22.imprint","INTERSECT",VERTEX,{"disambiguationData":[OD(0.0)],"derivedFrom":[subQ1,subQ0]});Q11=makeQuery(id+"F22.imprint","IMPRINT",FACE,{"disambiguationData":[TD([[makeQuery(id+"F22.imprint","IMPRINT",EDGE,{"disambiguationData":[TD([[subQ2,-1.0]])],"derivedFrom":subQ1}),1.0]])]});}
            var Q12;
            {var subQ0=sQuery(id+"F22.wireOp",EDGE,"E27");var subQ1=sQuery(id+"F22.wireOp",EDGE,"E21");var subQ2=makeQuery(id+"F22.imprint","INTERSECT",VERTEX,{"disambiguationData":[OD(0.0)],"derivedFrom":[subQ1,subQ0]});Q12=makeQuery(id+"F22.imprint","IMPRINT",FACE,{"disambiguationData":[TD([[makeQuery(id+"F22.imprint","IMPRINT",EDGE,{"disambiguationData":[TD([[subQ2,-1.0]])],"derivedFrom":subQ1}),1.0]])]});}
            var Q13;
            {var subQ0=sQuery(id+"F22.wireOp",EDGE,"E28");var subQ1=sQuery(id+"F22.wireOp",EDGE,"E21");var subQ2=makeQuery(id+"F22.imprint","INTERSECT",VERTEX,{"disambiguationData":[OD(1.0)],"derivedFrom":[subQ1,subQ0]});Q13=makeQuery(id+"F22.imprint","IMPRINT",FACE,{"disambiguationData":[TD([[makeQuery(id+"F22.imprint","IMPRINT",EDGE,{"disambiguationData":[TD([[subQ2,-1.0]])],"derivedFrom":subQ1}),1.0]])]});}
            var Q14;
            {var subQ0=sQuery(id+"F22.wireOp",EDGE,"E26");var subQ1=sQuery(id+"F22.wireOp",EDGE,"E21");var subQ2=makeQuery(id+"F22.imprint","INTERSECT",VERTEX,{"disambiguationData":[OD(0.0)],"derivedFrom":[subQ1,subQ0]});Q14=makeQuery(id+"F22.imprint","IMPRINT",FACE,{"disambiguationData":[TD([[makeQuery(id+"F22.imprint","IMPRINT",EDGE,{"disambiguationData":[TD([[subQ2,-1.0]])],"derivedFrom":subQ1}),1.0]])]});}
            var Q15;
            {var subQ0=sQuery(id+"F22.wireOp",EDGE,"E27");var subQ1=sQuery(id+"F22.wireOp",EDGE,"E26");var subQ2=makeQuery(id+"F22.imprint","INTERSECT",VERTEX,{"disambiguationData":[OD(1.0)],"derivedFrom":[subQ1,subQ0]});Q15=makeQuery(id+"F22.imprint","IMPRINT",FACE,{"disambiguationData":[TD([[makeQuery(id+"F22.imprint","IMPRINT",EDGE,{"disambiguationData":[TD([[subQ2,-1.0]])],"derivedFrom":subQ1}),1.0]])]});}
            extrude(context, id + "F23", {"entities" : qUnion([Q0, Q1, Q2, Q3, Q4, Q5, Q6, Q7, Q8, Q9, Q10, Q11, Q12, Q13, Q14, Q15]), "operationType" : NewBodyOperationType.ADD, "depth" : 3 * mm, "offsetDistance" : 25 * mm});
        }
    });
